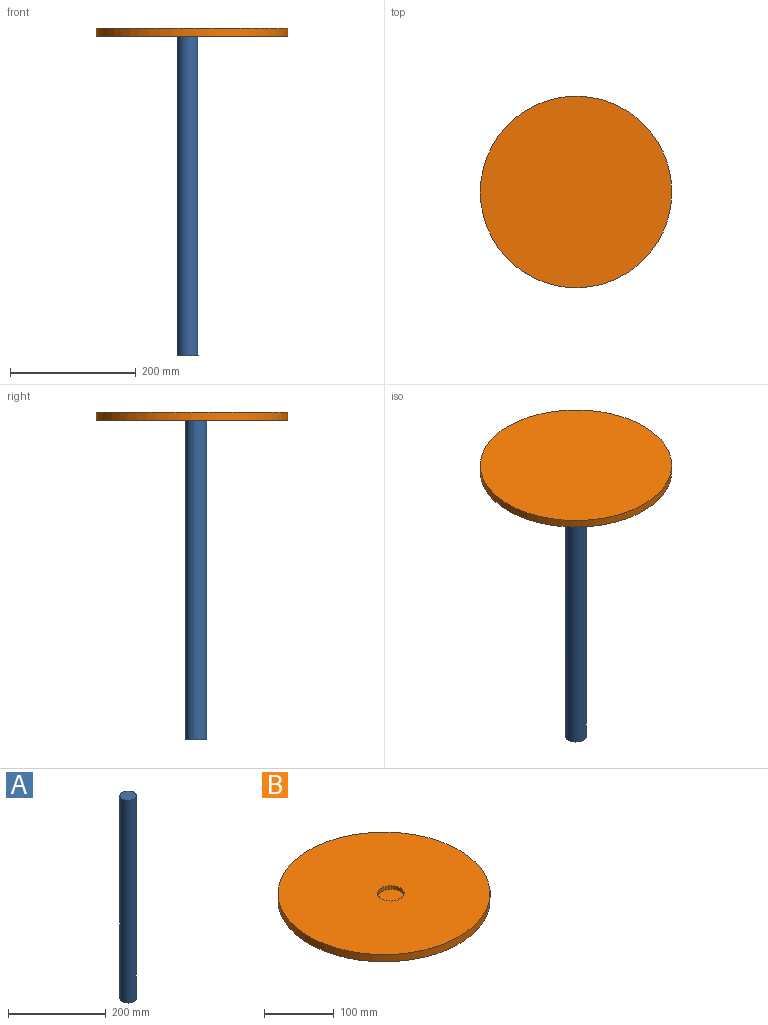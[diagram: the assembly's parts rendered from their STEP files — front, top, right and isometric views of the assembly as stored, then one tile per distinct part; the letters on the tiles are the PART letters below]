
ASSEMBLY  parts=2 mates=1
PART A: 3 faces, bbox 33.5x33.5x508 mm
  f0: cylinder r=16.74mm len=508mm, axis (0,0,-1), area 53427.2mm2, adj f1,f2
  f1: plane 33.48x33.48mm, normal (0,0,1), area 880.2mm2, adj f0
  f2: plane 33.48x33.48mm, normal (0,0,-1), area 880.2mm2, adj f0
PART B: 5 faces, bbox 304.8x304.8x12.7 mm
  f0: cylinder r=152.4mm len=304.8mm, axis (0,0,-1), area 12161mm2, adj f1,f2
  f1: plane 304.8x304.8mm, normal (0,0,1), area 71825.8mm2, adj f0,f3
  f2: plane 304.8x304.8mm, normal (0,0,-1), area 72965.9mm2, adj f0
  f3: cylinder r=19.05mm len=38.1mm, axis (0,0,1), area 760.1mm2, adj f1,f4
  f4: plane 38.1x38.1mm, normal (0,0,1), area 1140.1mm2, adj f3
PLACE A rot(axis=(0,-1,0),180deg) t=(80.72,-168.5,-47.67)mm
PLACE B rot(axis=(0,-1,0),180deg) t=(87.62,-161.64,-34.97)mm
MATE fastened A.f0 <-> B.f3  axis (0,0,1) through (80.72,-168.5,-47.67)mm
